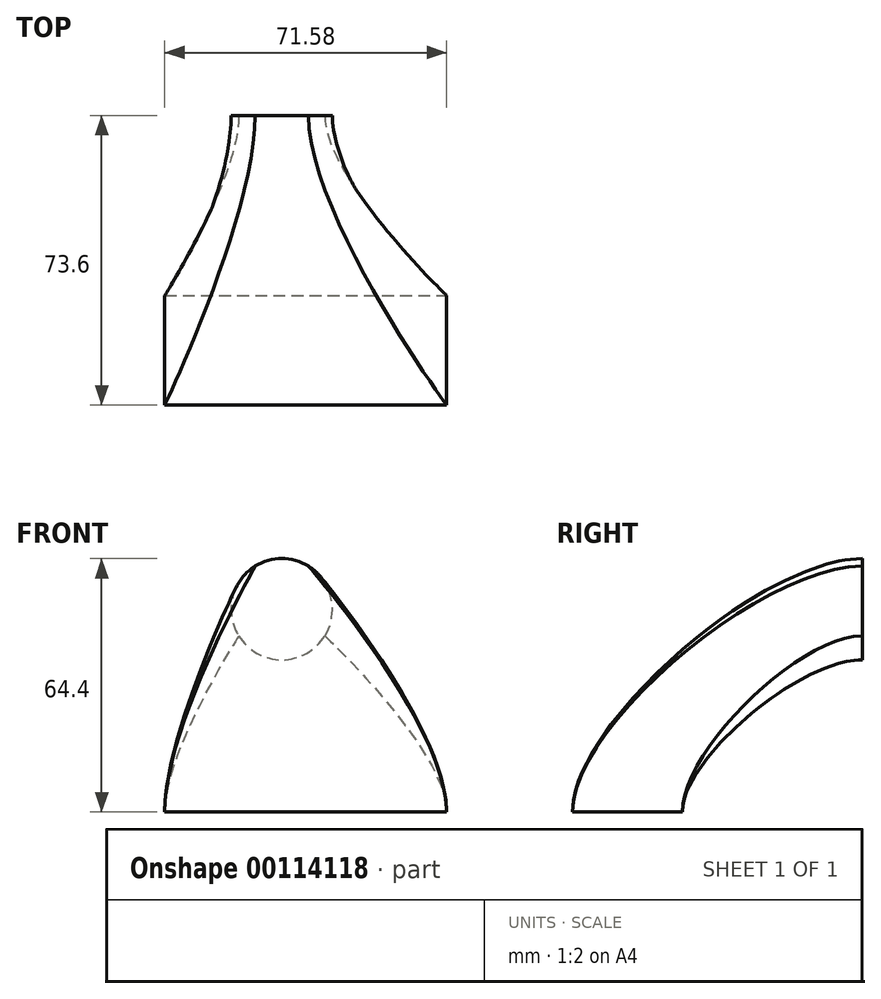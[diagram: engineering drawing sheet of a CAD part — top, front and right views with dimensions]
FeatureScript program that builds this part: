
annotation { "Feature Type Name" : "Feature", "Feature Type Description" : "" }
export const myFeature = defineFeature(function(context is Context, id is Id, definition is map)
    precondition{}
    {
        {
            var Q0;
            Q0=qCreatedBy(makeId("Front.planeOp"),FACE);
            var sketch = newSketch(context, id + "F0", { "sketchPlane" : qUnion([Q0])});
            skArc(sketch, "E0", {"start": v(6.78, 62.47) * mm, "mid": v(0, 64.4) * mm, "end": v(-6.78, 62.47) * mm});
            skArc(sketch, "E1", {"start": v(10.93, 44.76) * mm, "mid": v(12.52, 54.48) * mm, "end": v(6.78, 62.47) * mm});
            skArc(sketch, "E2", {"start": v(-6.78, 62.47) * mm, "mid": v(-12.52, 54.48) * mm, "end": v(-10.93, 44.76) * mm});
            skArc(sketch, "E3", {"start": v(-10.93, 44.76) * mm, "mid": v(0, 38.68) * mm, "end": v(10.93, 44.76) * mm});
            skSolve(sketch);
        }
        {
            var Q0;
            Q0=qCreatedBy(makeId("Top.planeOp"),FACE);
            var sketch = newSketch(context, id + "F1", { "sketchPlane" : qUnion([Q0])});
            skLineSegment(sketch, "E4.bottom", {"start": v(-29.73, -73.6) * mm, "end": v(41.85, -73.6) * mm});
            skLineSegment(sketch, "E4.top", {"start": v(-29.73, -45.72) * mm, "end": v(41.85, -45.72) * mm});
            skLineSegment(sketch, "E4.left", {"start": v(-29.73, -73.6) * mm, "end": v(-29.73, -45.72) * mm});
            skLineSegment(sketch, "E4.right", {"start": v(41.85, -73.6) * mm, "end": v(41.85, -45.72) * mm});
            skSolve(sketch);
        }
        {
            var Q0;
            Q0 = qSketchRegion(id + "F0", true);
            var Q1;
            Q1 = qSketchRegion(id + "F1", true);
            var Q2;
            Q2=sQuery(id+"F1.wireOp",VERTEX,"E4.right.end");
            var Q3;
            Q3=sQuery(id+"F0.wireOp",VERTEX,"E3.end");
            loft(context, id + "F2", {"startCondition" : LoftEndDerivativeType.NORMAL_TO_PROFILE, "startMagnitude" : 1, "endCondition" : LoftEndDerivativeType.NORMAL_TO_PROFILE, "endMagnitude" : 1, "sheetProfilesArray" : [{ "sheetProfileEntities" : qUnion([Q0]) }, { "sheetProfileEntities" : qUnion([Q1]) }], "connections" : [{ "connectionEntities" : qUnion([Q2, Q3]), "connectionEdgeQueries" : qUnion([]), "connectionEdgeParameters" : [] }]});
        }
    });
